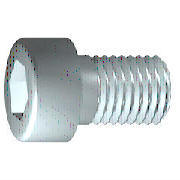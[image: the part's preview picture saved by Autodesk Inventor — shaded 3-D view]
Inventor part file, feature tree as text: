
AUTODESK INVENTOR PART (.ipt)
format: ipt  version: 2021 (Build 250183000, 183)  size: 194,560 bytes
history: native  units: mm (DEFAULTED — no unit token found)
features: sketch x2, extrude x1, plane x1, fillet x1
ambient origin geometry x7: Origin, YZ Plane, XY Plane, X Axis, Y Axis, Z Axis, Center Point
bodies: Solid1 (feature_tree), Body (feature_tree)
feature tree (5):
  extrude  "Slot"  Depth=6.0mm
  plane  "Work Plane1"
  fillet  "Fillet2"  Radius=6.0mm
  sketch  "Sketch1"  dims[d1=17.5mm d2=0.61355mm d3=6.0mm]
  sketch  "Sketch2"  dims[d4=3.0mm d5=60.0deg d6=6.0mm d7=6.0mm d8=5.773503mm d9=10.0mm d10=90.0deg d11=10.0mm d12=0.0mm d13=17.5mm d14=0.0mm d15=0.61345mm d16=0.61345mm d17=0.6mm d19=0.0mm d26=20.0mm d27=45.0deg d28=0.0mm d29=0.0mm d30=0.1mm]
